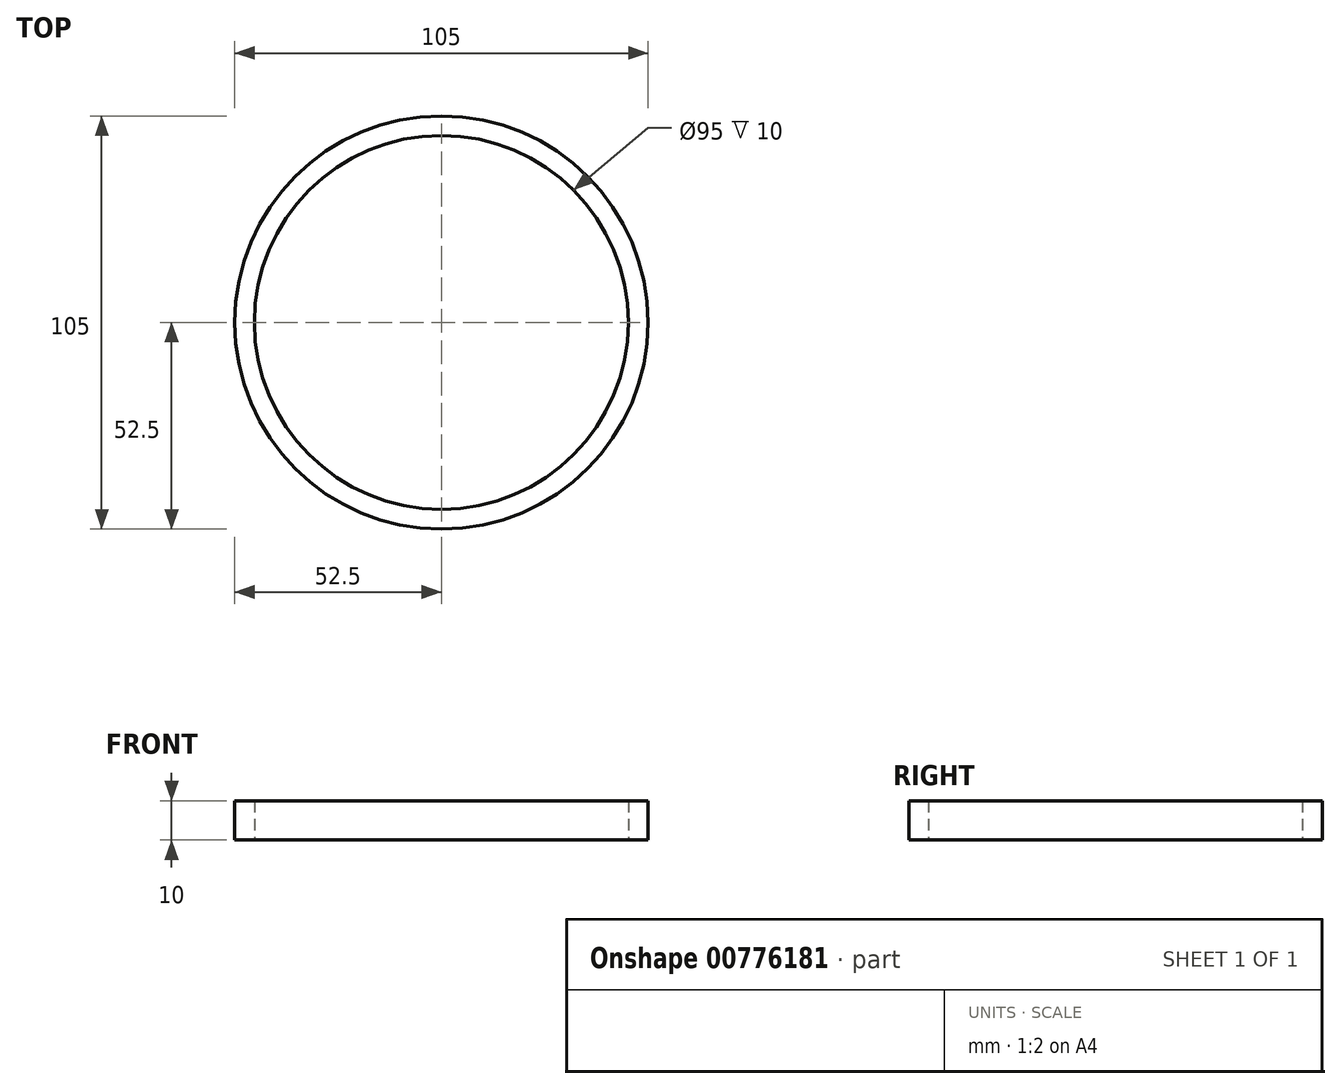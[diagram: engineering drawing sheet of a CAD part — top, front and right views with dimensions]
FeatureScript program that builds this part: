
annotation { "Feature Type Name" : "Feature", "Feature Type Description" : "" }
export const myFeature = defineFeature(function(context is Context, id is Id, definition is map)
    precondition{}
    {
        {
            var Q0;
            Q0=qCreatedBy(makeId("Top.planeOp"),FACE);
            var sketch = newSketch(context, id + "F0", { "sketchPlane" : qUnion([Q0])});
            skCircle(sketch, "E0", {"center": v(0, 0) * mm, "radius": 47.5 * mm});
            skCircle(sketch, "E1", {"center": v(0, 0) * mm, "radius": 52.5 * mm});
            skSolve(sketch);
        }
        {
            var Q0;
            Q0=makeQuery(id+"F0.imprint","IMPRINT",FACE,{"disambiguationData":[TD([[makeQuery(id+"F0.imprint","IMPRINT",EDGE,{"derivedFrom":sQuery(id+"F0.wireOp",EDGE,"E0")}),-1.0]])]});
            extrude(context, id + "F1", {"entities" : qUnion([Q0]), "depth" : 10 * mm, "offsetDistance" : 25 * mm});
        }
    });
